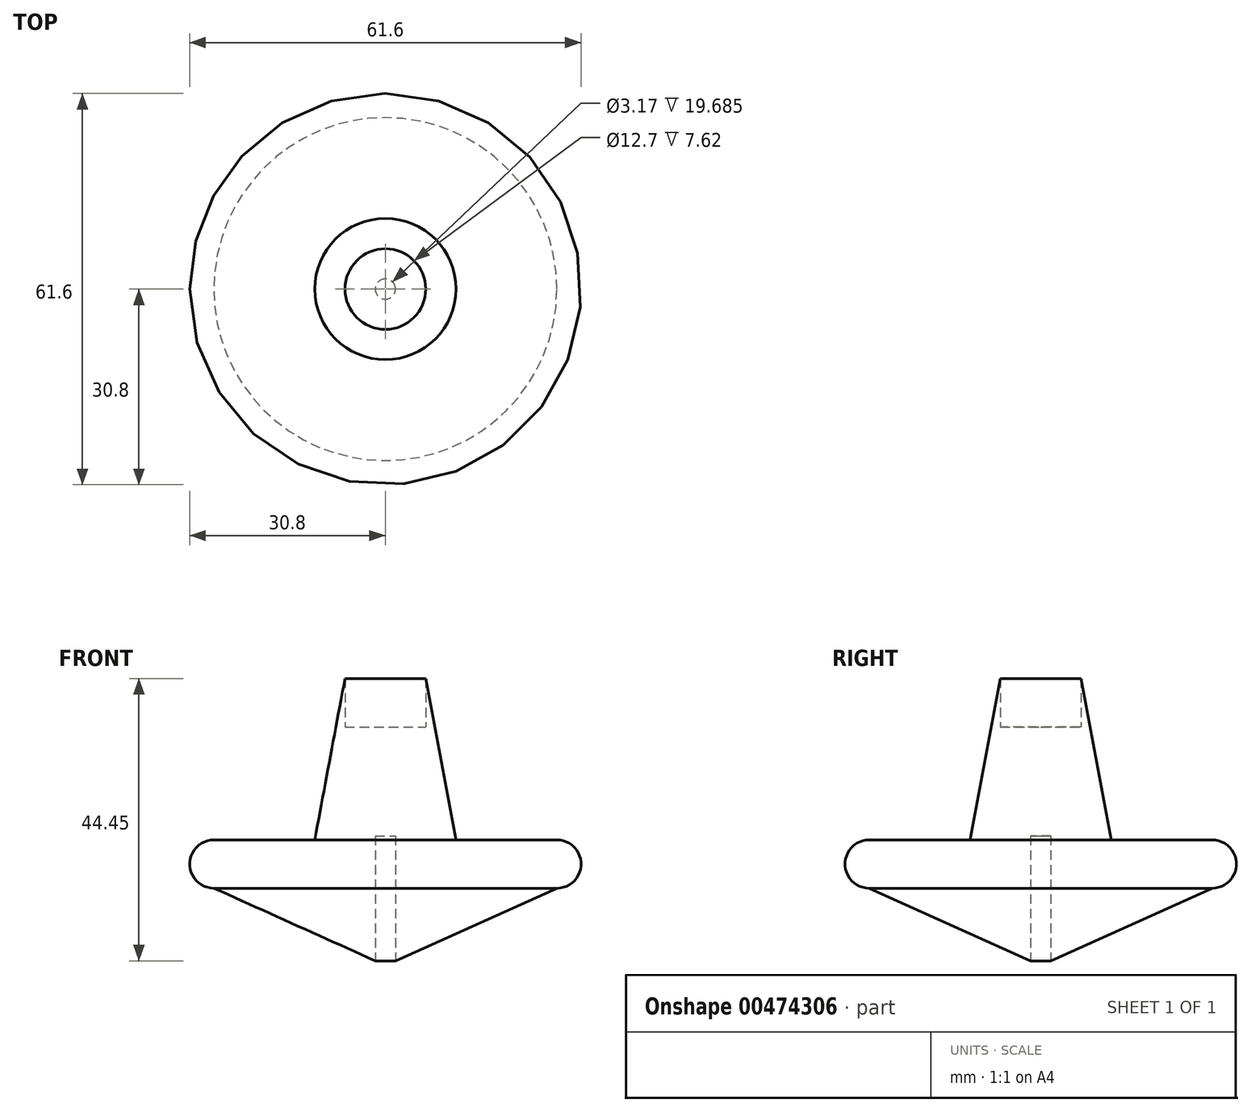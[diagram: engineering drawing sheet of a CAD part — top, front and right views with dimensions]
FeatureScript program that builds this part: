
annotation { "Feature Type Name" : "Feature", "Feature Type Description" : "" }
export const myFeature = defineFeature(function(context is Context, id is Id, definition is map)
    precondition{}
    {
        {
            var Q0;
            Q0=qCreatedBy(makeId("Front.planeOp"),FACE);
            var sketch = newSketch(context, id + "F0", { "sketchPlane" : qUnion([Q0])});
            skLineSegment(sketch, "E0", {"start": v(0, 0) * mm, "end": v(1.59, 0) * mm});
            skArc(sketch, "E1", {"start": v(26.99, 11.43) * mm, "mid": v(30.8, 15.24) * mm, "end": v(26.99, 19.05) * mm});
            skLineSegment(sketch, "E2", {"start": v(26.99, 11.43) * mm, "end": v(1.59, 0) * mm});
            skLineSegment(sketch, "E3", {"start": v(6.35, 44.45) * mm, "end": v(11.11, 19.05) * mm});
            skLineSegment(sketch, "E4", {"start": v(1.59, 0) * mm, "end": v(1.59, 19.69) * mm});
            skLineSegment(sketch, "E5", {"start": v(1.59, 19.69) * mm, "end": v(0, 19.69) * mm});
            skLineSegment(sketch, "E6", {"start": v(0, 19.69) * mm, "end": v(0, 31.75) * mm});
            skLineSegment(sketch, "E7", {"start": v(6.35, 44.45) * mm, "end": v(6.35, 36.83) * mm});
            skLineSegment(sketch, "E8", {"start": v(6.35, 36.83) * mm, "end": v(0, 36.83) * mm});
            skLineSegment(sketch, "E9", {"start": v(0, 36.83) * mm, "end": v(0, 31.75) * mm});
            skLineSegment(sketch, "E10", {"start": v(11.11, 19.05) * mm, "end": v(26.99, 19.05) * mm});
            skSolve(sketch);
        }
        {
            var Q0;
            Q0=makeQuery(id+"F0.imprint","IMPRINT",FACE,{"disambiguationData":[TD([[makeQuery(id+"F0.imprint","IMPRINT",EDGE,{"derivedFrom":sQuery(id+"F0.wireOp",EDGE,"E1")}),1.0]])]});
            var Q1;
            Q1=sQuery(id+"F0.wireOp",EDGE,"E6");
            revolve(context, id + "F1", {"entities" : qUnion([Q0]), "axis" : qUnion([Q1]), "revolveType" : RevolveType.FULL});
        }
    });
